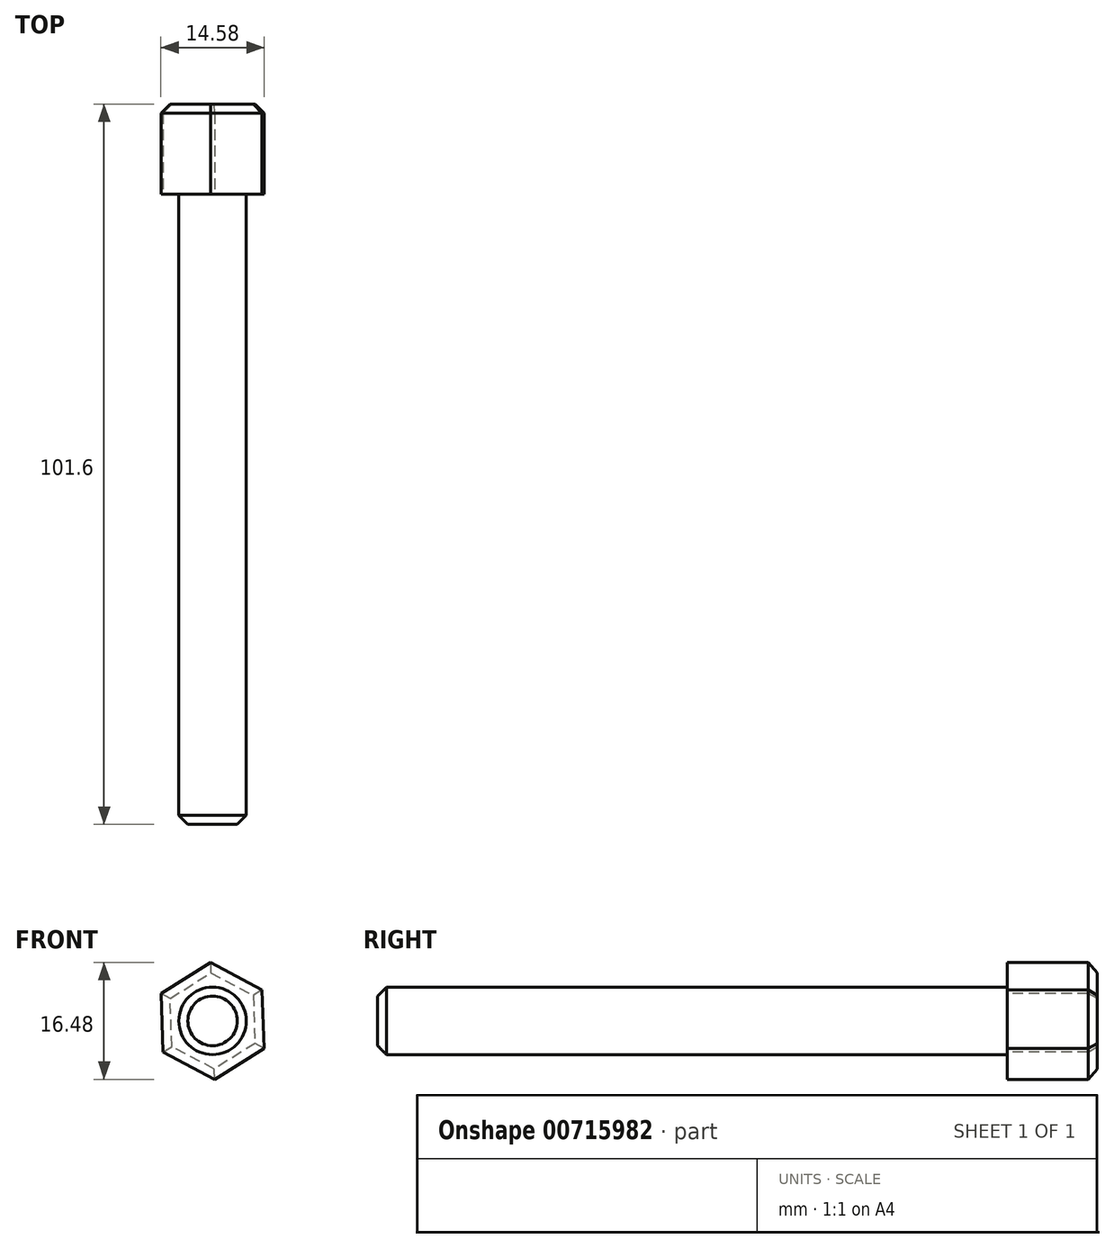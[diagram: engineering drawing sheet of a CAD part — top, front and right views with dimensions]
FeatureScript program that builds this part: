
annotation { "Feature Type Name" : "Feature", "Feature Type Description" : "" }
export const myFeature = defineFeature(function(context is Context, id is Id, definition is map)
    precondition{}
    {
        {
            var Q0;
            Q0=qCreatedBy(makeId("Front.planeOp"),FACE);
            var sketch = newSketch(context, id + "F0", { "sketchPlane" : qUnion([Q0])});
            skCircle(sketch, "E0.cCircle", {"center": v(0, 0) * mm, "radius": 7.14 * mm, "construction": true});
            skLineSegment(sketch, "E0.0", {"start": v(-7.29, 3.86) * mm, "end": v(-0.3, 8.24) * mm});
            skLineSegment(sketch, "E0.1", {"start": v(-0.3, 8.24) * mm, "end": v(7, 4.38) * mm});
            skLineSegment(sketch, "E0.2", {"start": v(7, 4.38) * mm, "end": v(7.29, -3.86) * mm});
            skLineSegment(sketch, "E0.3", {"start": v(7.29, -3.86) * mm, "end": v(0.3, -8.24) * mm});
            skLineSegment(sketch, "E0.4", {"start": v(0.3, -8.24) * mm, "end": v(-7, -4.38) * mm});
            skLineSegment(sketch, "E0.5", {"start": v(-7, -4.38) * mm, "end": v(-7.29, 3.86) * mm});
            skPoint(sketch, "E0.0.midPoint", {"position": v(-3.8, 6.05) * mm});
            skSolve(sketch);
        }
        {
            var Q0;
            Q0 = qSketchRegion(id + "F0", true);
            var Q1;
            Q1=makeQuery(id+"F0.imprint","IMPRINT",FACE,{"disambiguationData":[TD([[makeQuery(id+"F0.imprint","IMPRINT",EDGE,{"derivedFrom":sQuery(id+"F0.wireOp",EDGE,"E0.0")}),-1.0]])]});
            extrude(context, id + "F1", {"entities" : qUnion([Q0, Q1]), "oppositeDirection" : true, "depth" : 12.7 * mm, "offsetDistance" : 25.4 * mm});
        }
        {
            var Q0;
            Q0=qCreatedBy(makeId("Front.planeOp"),FACE);
            var sketch = newSketch(context, id + "F2", { "sketchPlane" : qUnion([Q0])});
            skCircle(sketch, "E1", {"center": v(0, 0) * mm, "radius": 4.76 * mm});
            skSolve(sketch);
        }
        {
            var Q0;
            Q0 = qSketchRegion(id + "F2", true);
            extrude(context, id + "F3", {"entities" : qUnion([Q0]), "operationType" : NewBodyOperationType.ADD, "depth" : 88.9 * mm, "offsetDistance" : 25.4 * mm});
        }
        {
            var Q0;
            Q0=makeQuery(id+"F3.opExtrude","CAP_EDGE",EDGE,{"disambiguationData":[OSD([sQuery(id+"F2.wireOp",EDGE,"E1")])],"isStart":false});
            var Q1;
            Q1=makeQuery(id+"F1.opExtrude","CAP_EDGE",EDGE,{"disambiguationData":[OSD([sQuery(id+"F0.wireOp",EDGE,"E0.5")])],"isStart":false});
            var Q2;
            Q2=makeQuery(id+"F1.opExtrude","CAP_EDGE",EDGE,{"disambiguationData":[OSD([sQuery(id+"F0.wireOp",EDGE,"E0.4")])],"isStart":false});
            var Q3;
            Q3=makeQuery(id+"F1.opExtrude","CAP_EDGE",EDGE,{"disambiguationData":[OSD([sQuery(id+"F0.wireOp",EDGE,"E0.3")])],"isStart":false});
            var Q4;
            Q4=makeQuery(id+"F1.opExtrude","CAP_EDGE",EDGE,{"disambiguationData":[OSD([sQuery(id+"F0.wireOp",EDGE,"E0.2")])],"isStart":false});
            var Q5;
            Q5=makeQuery(id+"F1.opExtrude","CAP_EDGE",EDGE,{"disambiguationData":[OSD([sQuery(id+"F0.wireOp",EDGE,"E0.1")])],"isStart":false});
            var Q6;
            Q6=makeQuery(id+"F1.opExtrude","CAP_EDGE",EDGE,{"disambiguationData":[OSD([sQuery(id+"F0.wireOp",EDGE,"E0.0")])],"isStart":false});
            chamfer(context, id + "F4", {"entities" : qUnion([Q0, Q1, Q2, Q3, Q4, Q5, Q6]), "width" : 1.27 * mm, "tangentPropagation" : true});
        }
    });
